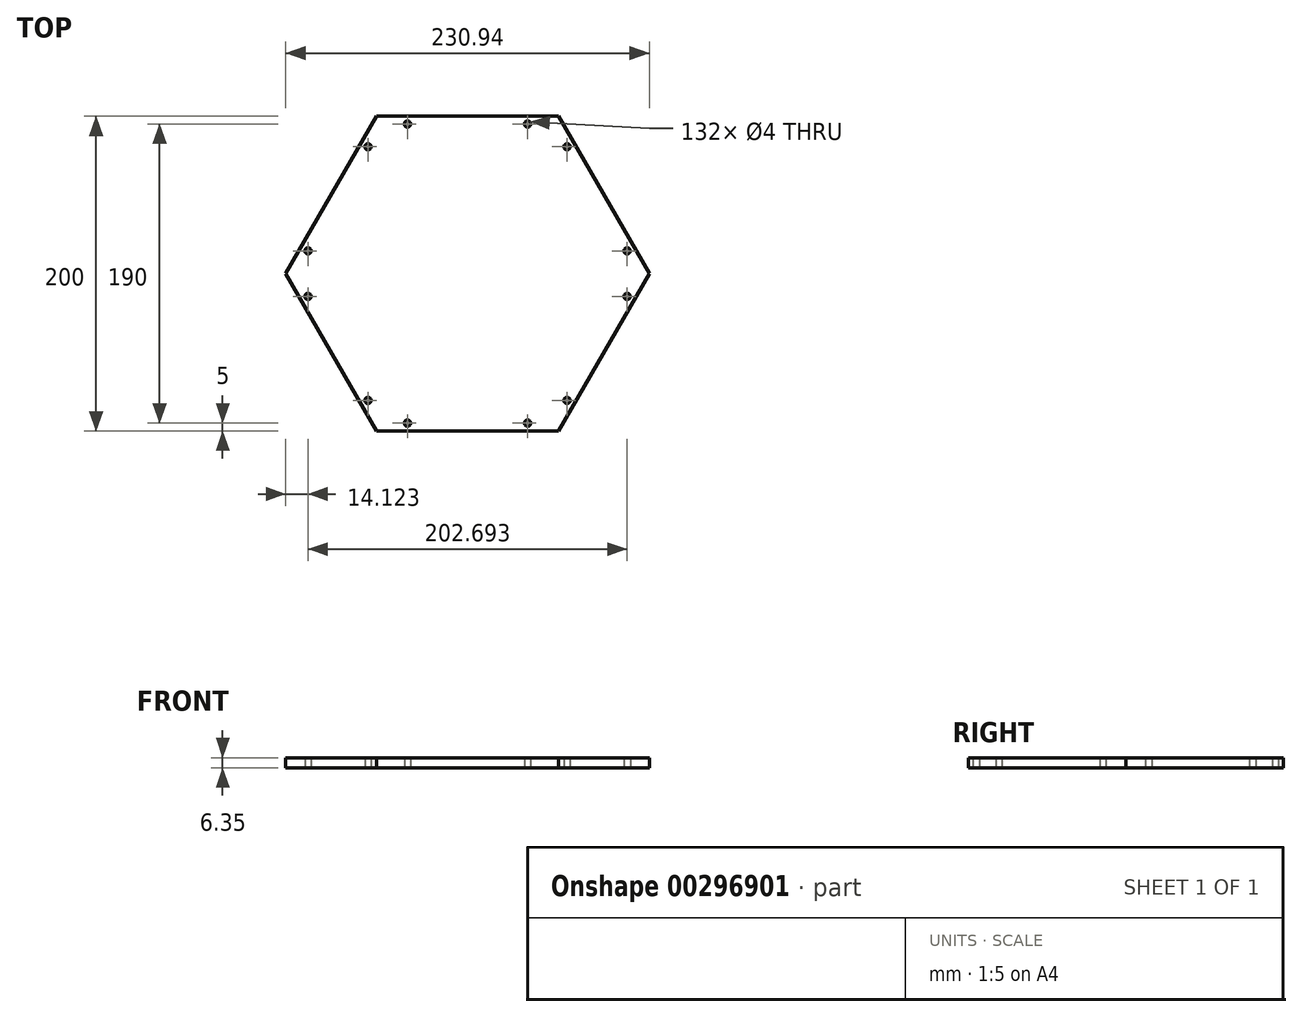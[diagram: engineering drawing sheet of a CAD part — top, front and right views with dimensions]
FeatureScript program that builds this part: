
annotation { "Feature Type Name" : "Feature", "Feature Type Description" : "" }
export const myFeature = defineFeature(function(context is Context, id is Id, definition is map)
    precondition{}
    {
        {
            var Q0;
            Q0=qCreatedBy(makeId("Top.planeOp"),FACE);
            var sketch = newSketch(context, id + "F0", { "sketchPlane" : qUnion([Q0])});
            skCircle(sketch, "E0", {"center": v(0, 0) * mm, "radius": 100 * mm});
            skCircle(sketch, "E1.cCircle", {"center": v(0, 0) * mm, "radius": 100 * mm, "construction": true});
            skLineSegment(sketch, "E1.0", {"start": v(-57.74, 100) * mm, "end": v(57.74, 100) * mm});
            skLineSegment(sketch, "E1.1", {"start": v(57.74, 100) * mm, "end": v(115.47, 0) * mm});
            skLineSegment(sketch, "E1.2", {"start": v(115.47, 0) * mm, "end": v(57.74, -100) * mm});
            skLineSegment(sketch, "E1.3", {"start": v(57.74, -100) * mm, "end": v(-57.74, -100) * mm});
            skLineSegment(sketch, "E1.4", {"start": v(-57.74, -100) * mm, "end": v(-115.47, 0) * mm});
            skLineSegment(sketch, "E1.5", {"start": v(-115.47, 0) * mm, "end": v(-57.74, 100) * mm});
            skPoint(sketch, "E1.0.midPoint", {"position": v(0, 100) * mm});
            skSolve(sketch);
        }
        {
            var Q0;
            Q0 = qSketchRegion(id + "F0", true);
            extrude(context, id + "F1", {"entities" : qUnion([Q0]), "depth" : 6.35 * mm});
        }
        {
            var Q0;
            Q0=qCreatedBy(makeId("Top.planeOp"),FACE);
            var sketch = newSketch(context, id + "F2", { "sketchPlane" : qUnion([Q0])});
            skCircle(sketch, "E2.cCircle", {"center": v(0, 0) * mm, "radius": 95 * mm, "construction": true});
            skLineSegment(sketch, "E2.0", {"start": v(-54.85, 95) * mm, "end": v(54.85, 95) * mm, "construction": true});
            skLineSegment(sketch, "E2.1", {"start": v(54.85, 95) * mm, "end": v(109.7, 0) * mm, "construction": true});
            skLineSegment(sketch, "E2.2", {"start": v(109.7, 0) * mm, "end": v(54.85, -95) * mm, "construction": true});
            skLineSegment(sketch, "E2.3", {"start": v(54.85, -95) * mm, "end": v(-54.85, -95) * mm, "construction": true});
            skLineSegment(sketch, "E2.4", {"start": v(-54.85, -95) * mm, "end": v(-109.7, 0) * mm, "construction": true});
            skLineSegment(sketch, "E2.5", {"start": v(-109.7, 0) * mm, "end": v(-54.85, 95) * mm, "construction": true});
            skPoint(sketch, "E2.0.midPoint", {"position": v(0, 95) * mm});
            skPoint(sketch, "E3", {"position": v(38.15, 95) * mm});
            skPoint(sketch, "E4", {"position": v(-38.15, 95) * mm});
            skPoint(sketch, "E5", {"position": v(38.15, -95) * mm});
            skPoint(sketch, "E6", {"position": v(-38.15, -95) * mm});
            skPoint(sketch, "E7", {"position": v(-63.2, -80.54) * mm});
            skPoint(sketch, "E8", {"position": v(-101.35, -14.46) * mm});
            skPoint(sketch, "E9", {"position": v(-101.35, 14.46) * mm});
            skPoint(sketch, "E10", {"position": v(-63.2, 80.54) * mm});
            skPoint(sketch, "E11", {"position": v(63.2, 80.54) * mm});
            skPoint(sketch, "E12", {"position": v(101.35, 14.46) * mm});
            skPoint(sketch, "E13", {"position": v(101.35, -14.46) * mm});
            skPoint(sketch, "E14", {"position": v(63.2, -80.54) * mm});
            skCircle(sketch, "E15", {"center": v(38.15, 95) * mm, "radius": 2 * mm});
            skCircle(sketch, "E16", {"center": v(-38.15, 95) * mm, "radius": 2 * mm});
            skCircle(sketch, "E17", {"center": v(-63.2, 80.54) * mm, "radius": 2 * mm});
            skCircle(sketch, "E18", {"center": v(-101.35, 14.46) * mm, "radius": 2 * mm});
            skCircle(sketch, "E19", {"center": v(-101.35, -14.46) * mm, "radius": 2 * mm});
            skCircle(sketch, "E20", {"center": v(-63.2, -80.54) * mm, "radius": 2 * mm});
            skCircle(sketch, "E21", {"center": v(-38.15, -95) * mm, "radius": 2 * mm});
            skCircle(sketch, "E22", {"center": v(38.15, -95) * mm, "radius": 2 * mm});
            skCircle(sketch, "E23", {"center": v(63.2, -80.54) * mm, "radius": 2 * mm});
            skCircle(sketch, "E24", {"center": v(101.35, -14.46) * mm, "radius": 2 * mm});
            skCircle(sketch, "E25", {"center": v(101.35, 14.46) * mm, "radius": 2 * mm});
            skCircle(sketch, "E26", {"center": v(63.2, 80.54) * mm, "radius": 2 * mm});
            skSolve(sketch);
        }
        {
            var Q0;
            Q0 = qSketchRegion(id + "F2", true);
            extrude(context, id + "F3", {"entities" : qUnion([Q0]), "operationType" : NewBodyOperationType.REMOVE, "depth" : 20000 * mm});
        }
    });
